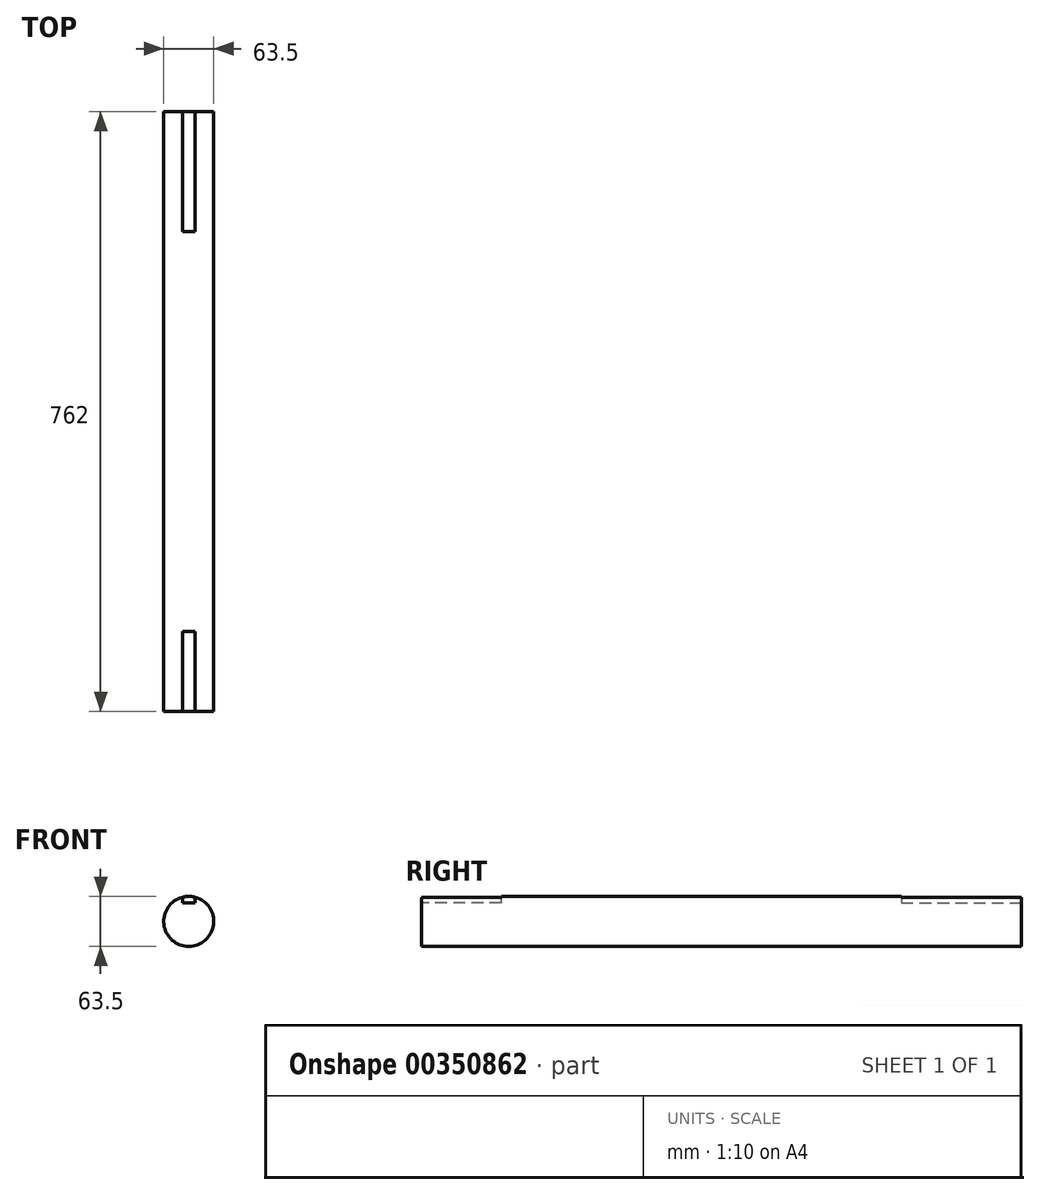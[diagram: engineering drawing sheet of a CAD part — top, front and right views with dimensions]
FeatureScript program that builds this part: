
annotation { "Feature Type Name" : "Feature", "Feature Type Description" : "" }
export const myFeature = defineFeature(function(context is Context, id is Id, definition is map)
    precondition{}
    {
        {
            var Q0;
            Q0=qCreatedBy(makeId("Front.planeOp"),FACE);
            var sketch = newSketch(context, id + "F0", { "sketchPlane" : qUnion([Q0])});
            skCircle(sketch, "E0", {"center": v(0, 0) * mm, "radius": 31.75 * mm});
            skLineSegment(sketch, "E1.bottom", {"start": v(7.94, 39.69) * mm, "end": v(-7.94, 39.69) * mm});
            skLineSegment(sketch, "E1.top", {"start": v(7.94, 23.81) * mm, "end": v(-7.94, 23.81) * mm});
            skLineSegment(sketch, "E1.left", {"start": v(7.94, 39.69) * mm, "end": v(7.94, 23.81) * mm});
            skLineSegment(sketch, "E1.right", {"start": v(-7.94, 39.69) * mm, "end": v(-7.94, 23.81) * mm});
            skPoint(sketch, "E1.middle", {"position": v(0, 31.75) * mm});
            skSolve(sketch);
        }
        {
            var Q0;
            {var subQ5=sQuery(id+"F0.wireOp",EDGE,"E1.top");Q0=makeQuery(id+"F0.imprint","IMPRINT",FACE,{"disambiguationData":[TD([[makeQuery(id+"F0.imprint","IMPRINT",EDGE,{"derivedFrom":subQ5}),1.0]])]});}
            var Q1;
            {var subQ5=sQuery(id+"F0.wireOp",EDGE,"E1.top");Q1=makeQuery(id+"F0.imprint","IMPRINT",FACE,{"disambiguationData":[TD([[makeQuery(id+"F0.imprint","IMPRINT",EDGE,{"derivedFrom":subQ5}),-1.0]])]});}
            var Q2;
            Q2=sQuery(id+"F0.wireOp",EDGE,"E0");
            extrude(context, id + "F1", {"entities" : qUnion([Q0, Q1]), "surfaceEntities" : qUnion([Q2]), "depth" : 762 * mm});
        }
        {
            var Q0;
            {var subQ5=sQuery(id+"F0.wireOp",EDGE,"E1.top");Q0=makeQuery(id+"F0.imprint","IMPRINT",FACE,{"disambiguationData":[TD([[makeQuery(id+"F0.imprint","IMPRINT",EDGE,{"derivedFrom":subQ5}),-1.0]])]});}
            extrude(context, id + "F2", {"entities" : qUnion([Q0]), "operationType" : NewBodyOperationType.REMOVE, "depth" : 152.4 * mm});
        }
        {
            var Q0;
            Q0=makeQuery(id+"F1.opExtrude","CAP_FACE",FACE,{"disambiguationData":[OSD([sQuery(id+"F0.wireOp",EDGE,"E0")])],"isStart":false});
            var sketch = newSketch(context, id + "F3", { "sketchPlane" : qUnion([Q0])});
            skLineSegment(sketch, "E2.bottom", {"start": v(7.94, 23.81) * mm, "end": v(-7.94, 23.81) * mm});
            skLineSegment(sketch, "E2.top", {"start": v(7.94, 39.69) * mm, "end": v(-7.94, 39.69) * mm});
            skLineSegment(sketch, "E2.left", {"start": v(7.94, 23.81) * mm, "end": v(7.94, 39.69) * mm});
            skLineSegment(sketch, "E2.right", {"start": v(-7.94, 23.81) * mm, "end": v(-7.94, 39.69) * mm});
            skPoint(sketch, "E2.middle", {"position": v(0, 31.75) * mm});
            skSolve(sketch);
        }
        {
            var Q0;
            {var subQ0=sQuery(id+"F3.wireOp",EDGE,"E2.bottom");Q0=makeQuery(id+"F3.imprint","IMPRINT",FACE,{"disambiguationData":[TD([[makeQuery(id+"F3.imprint","IMPRINT",EDGE,{"derivedFrom":subQ0}),-1.0]])]});}
            extrude(context, id + "F4", {"entities" : qUnion([Q0]), "operationType" : NewBodyOperationType.REMOVE, "oppositeDirection" : true, "depth" : 101.6 * mm});
        }
    });
